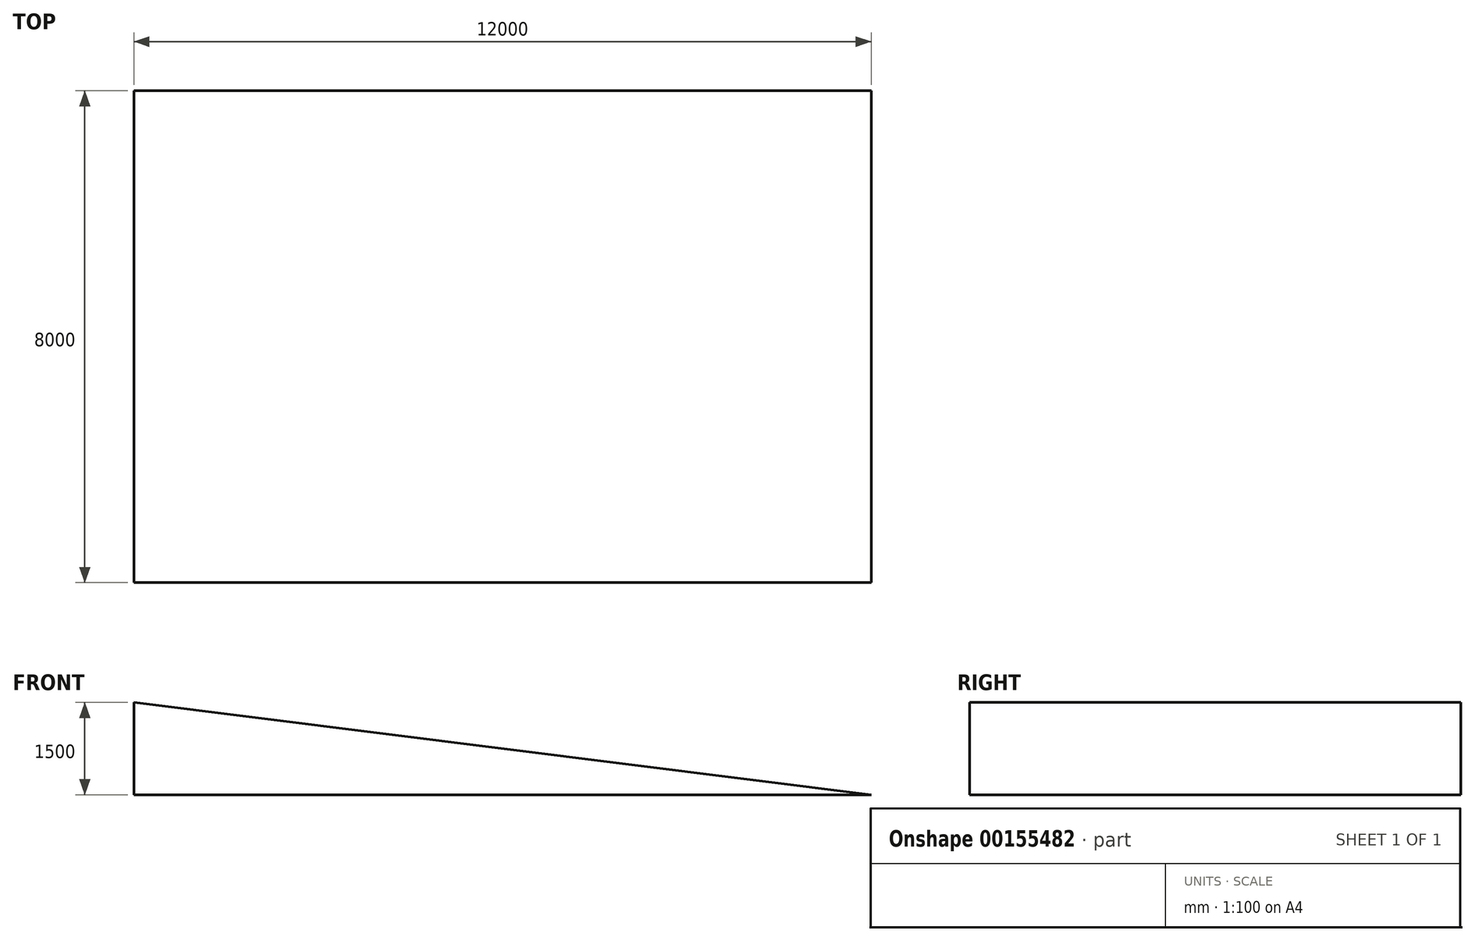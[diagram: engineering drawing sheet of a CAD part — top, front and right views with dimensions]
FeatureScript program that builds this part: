
annotation { "Feature Type Name" : "Feature", "Feature Type Description" : "" }
export const myFeature = defineFeature(function(context is Context, id is Id, definition is map)
    precondition{}
    {
        {
            var Q0;
            Q0=qCreatedBy(makeId("Front.planeOp"),FACE);
            var sketch = newSketch(context, id + "F0", { "sketchPlane" : qUnion([Q0])});
            skLineSegment(sketch, "E0", {"start": v(0, 1500) * mm, "end": v(0, 0) * mm});
            skLineSegment(sketch, "E1", {"start": v(12000, 0) * mm, "end": v(0, 0) * mm});
            skLineSegment(sketch, "E2", {"start": v(12000, 0) * mm, "end": v(0, 1500) * mm});
            skSolve(sketch);
        }
        {
            var Q0;
            Q0=makeQuery(id+"F0.imprint","IMPRINT",FACE,{"disambiguationData":[TD([[makeQuery(id+"F0.imprint","IMPRINT",EDGE,{"derivedFrom":sQuery(id+"F0.wireOp",EDGE,"E0")}),1.0]])]});
            extrude(context, id + "F1", {"entities" : qUnion([Q0]), "depth" : 8000 * mm});
        }
    });
